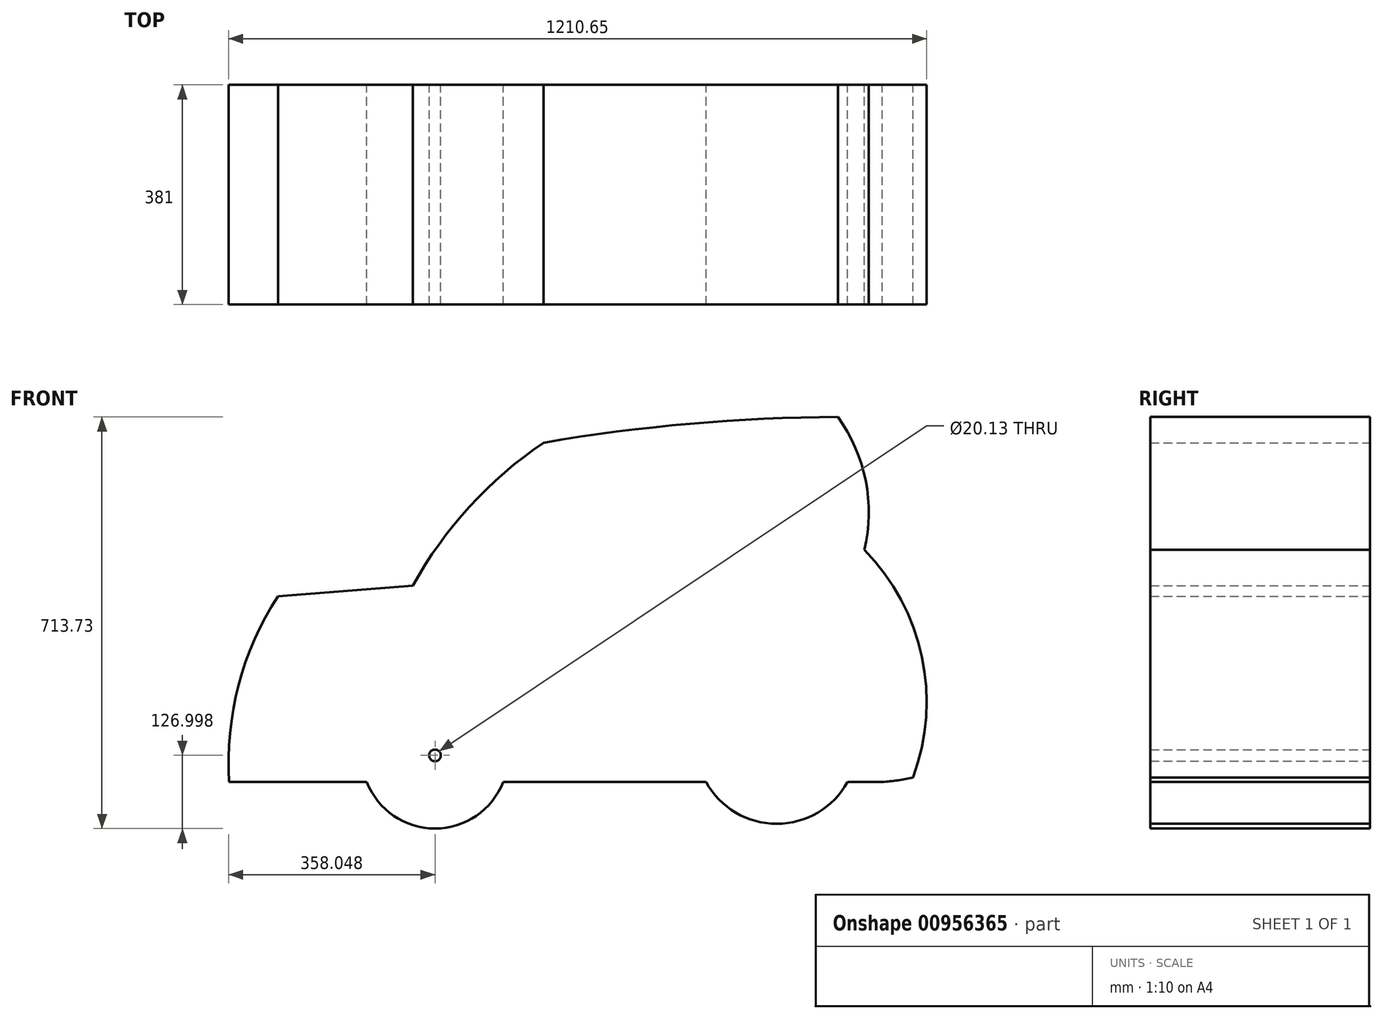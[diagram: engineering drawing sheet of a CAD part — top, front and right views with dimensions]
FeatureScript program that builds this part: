
annotation { "Feature Type Name" : "Feature", "Feature Type Description" : "" }
export const myFeature = defineFeature(function(context is Context, id is Id, definition is map)
    precondition{}
    {
        {
            var Q0;
            Q0=qCreatedBy(makeId("Front.planeOp"),FACE);
            var sketch = newSketch(context, id + "F0", { "sketchPlane" : qUnion([Q0])});
            skLineSegment(sketch, "E0", {"start": v(-550.06, -402.5) * mm, "end": v(587.59, -402.5) * mm});
            skArc(sketch, "E1", {"start": v(-460.42, -80.35) * mm, "mid": v(-528.74, -234.59) * mm, "end": v(-545.09, -402.5) * mm});
            skPoint(sketch, "E2.left.start.orphan", {"position": v(-546.14, 0) * mm});
            skLineSegment(sketch, "E3", {"start": v(-460.42, -80.35) * mm, "end": v(556.37, 0) * mm});
            skPoint(sketch, "E4.orphan", {"position": v(-396.2, 0) * mm});
            skArc(sketch, "E5", {"start": v(587.59, -402.5) * mm, "mid": v(614.29, -399.52) * mm, "end": v(640.73, -394.79) * mm});
            skArc(sketch, "E6", {"start": v(640.73, -394.79) * mm, "mid": v(656.24, -185.07) * mm, "end": v(556.37, 0) * mm});
            skArc(sketch, "E7", {"start": v(0, 185.97) * mm, "mid": v(-127.81, 75.33) * mm, "end": v(-226.57, -61.87) * mm});
            skArc(sketch, "E8", {"start": v(556.37, 0) * mm, "mid": v(558.75, 120.31) * mm, "end": v(510.46, 230.54) * mm});
            skArc(sketch, "E9", {"start": v(510.46, 230.54) * mm, "mid": v(254.3, 218.9) * mm, "end": v(0, 185.97) * mm});
            skArc(sketch, "E10", {"start": v(-506.76, -209.66) * mm, "mid": v(-445.36, -152.31) * mm, "end": v(-409.5, -76.33) * mm});
            skArc(sketch, "E11", {"start": v(-476.34, -152.31) * mm, "mid": v(-503.32, -174.74) * mm, "end": v(-506.76, -209.66) * mm});
            skPoint(sketch, "E11.startSnap0", {"position": v(-445.36, -152.31) * mm});
            skCircle(sketch, "E12", {"center": v(-188.1, -356.2) * mm, "radius": 127 * mm});
            skCircle(sketch, "E13", {"center": v(-188.1, -356.2) * mm, "radius": 10.07 * mm});
            skCircle(sketch, "E14", {"center": v(404.55, -334.73) * mm, "radius": 140.1 * mm});
            skSolve(sketch);
        }
        {
            var Q0;
            {var subQ5=sQuery(id+"F0.wireOp",EDGE,"E1");Q0=makeQuery(id+"F0.imprint","IMPRINT",FACE,{"disambiguationData":[TD([[makeQuery(id+"F0.imprint","IMPRINT",EDGE,{"derivedFrom":subQ5}),1.0]])]});}
            var Q1;
            {var subQ2=sQuery(id+"F0.wireOp",EDGE,"E7");Q1=makeQuery(id+"F0.imprint","IMPRINT",FACE,{"disambiguationData":[TD([[makeQuery(id+"F0.imprint","IMPRINT",EDGE,{"derivedFrom":subQ2}),1.0]])]});}
            var Q2;
            Q2 = qSketchRegion(id + "F0", true);
            var Q3;
            Q3=makeQuery(id+"F0.imprint","IMPRINT",FACE,{"disambiguationData":[TD([[makeQuery(id+"F0.imprint","IMPRINT",EDGE,{"derivedFrom":sQuery(id+"F0.wireOp",EDGE,"E13")}),-1.0]])]});
            var Q4;
            {var subQ0=sQuery(id+"F0.wireOp",EDGE,"E12");var subQ1=sQuery(id+"F0.wireOp",EDGE,"E0");var subQ2=makeQuery(id+"F0.imprint","INTERSECT",VERTEX,{"disambiguationData":[OD(0.0)],"derivedFrom":[subQ1,subQ0]});Q4=makeQuery(id+"F0.imprint","IMPRINT",FACE,{"disambiguationData":[TD([[makeQuery(id+"F0.imprint","IMPRINT",EDGE,{"disambiguationData":[TD([[subQ2,-1.0]])],"derivedFrom":subQ1}),-1.0]])]});}
            var Q5;
            {var subQ0=sQuery(id+"F0.wireOp",EDGE,"E14");var subQ1=sQuery(id+"F0.wireOp",EDGE,"E0");var subQ2=makeQuery(id+"F0.imprint","INTERSECT",VERTEX,{"disambiguationData":[OD(0.0)],"derivedFrom":[subQ1,subQ0]});Q5=makeQuery(id+"F0.imprint","IMPRINT",FACE,{"disambiguationData":[TD([[makeQuery(id+"F0.imprint","IMPRINT",EDGE,{"disambiguationData":[TD([[subQ2,-1.0]])],"derivedFrom":subQ1}),1.0]])]});}
            var Q6;
            {var subQ0=sQuery(id+"F0.wireOp",EDGE,"E14");var subQ1=sQuery(id+"F0.wireOp",EDGE,"E0");var subQ2=makeQuery(id+"F0.imprint","INTERSECT",VERTEX,{"disambiguationData":[OD(0.0)],"derivedFrom":[subQ1,subQ0]});Q6=makeQuery(id+"F0.imprint","IMPRINT",FACE,{"disambiguationData":[TD([[makeQuery(id+"F0.imprint","IMPRINT",EDGE,{"disambiguationData":[TD([[subQ2,-1.0]])],"derivedFrom":subQ1}),-1.0]])]});}
            extrude(context, id + "F1", {"entities" : qUnion([Q0, Q1, Q2, Q3, Q4, Q5, Q6]), "depth" : 381 * mm, "offsetDistance" : 25.4 * mm});
        }
    });
